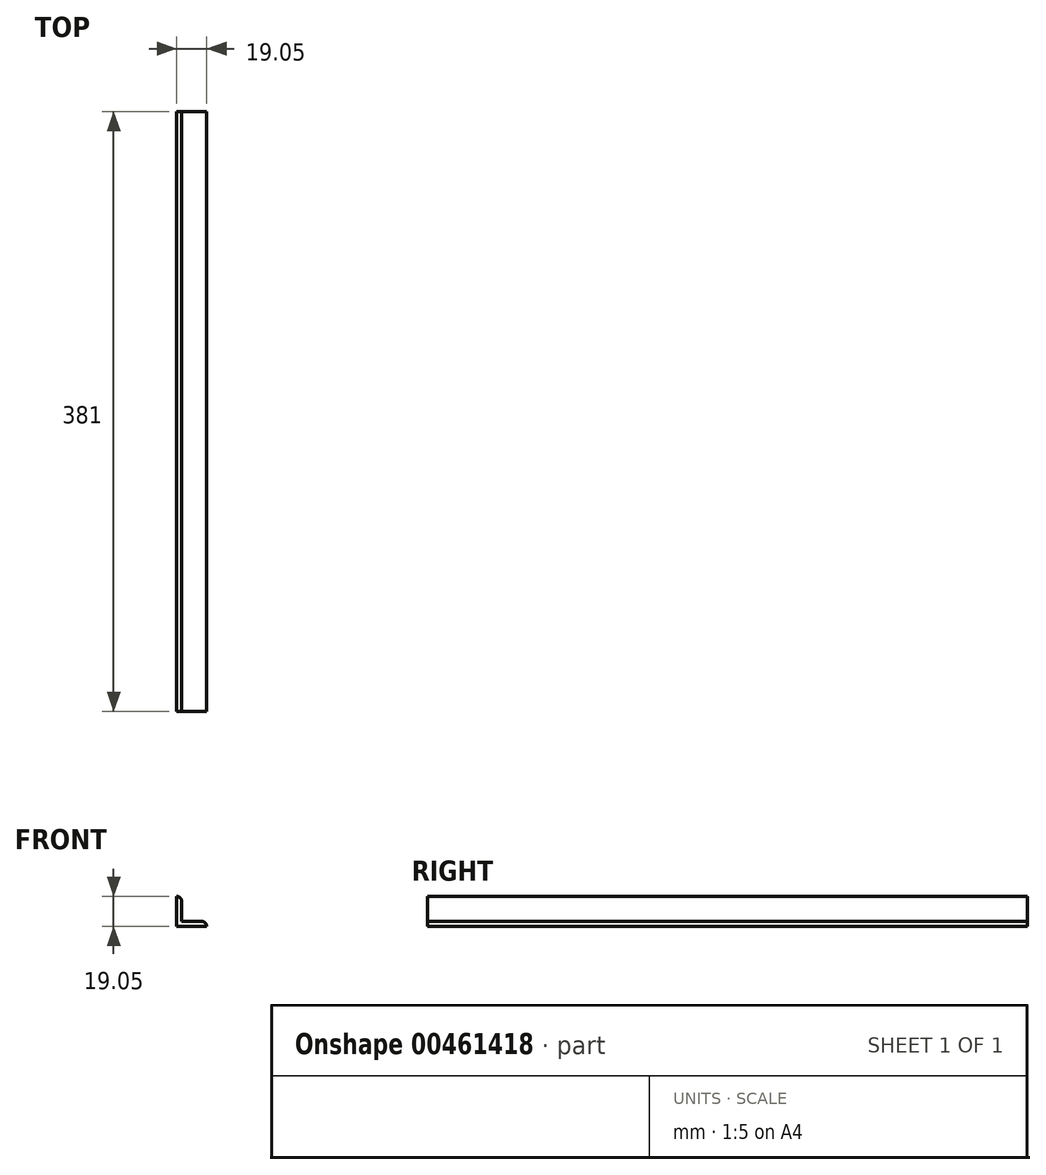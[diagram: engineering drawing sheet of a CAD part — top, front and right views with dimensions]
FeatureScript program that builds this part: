
annotation { "Feature Type Name" : "Feature", "Feature Type Description" : "" }
export const myFeature = defineFeature(function(context is Context, id is Id, definition is map)
    precondition{}
    {
        {
            var Q0;
            Q0=qCreatedBy(makeId("Front.planeOp"),FACE);
            var sketch = newSketch(context, id + "F0", { "sketchPlane" : qUnion([Q0])});
            skLineSegment(sketch, "E0", {"start": v(0, 19.05) * mm, "end": v(0, 0) * mm});
            skLineSegment(sketch, "E1", {"start": v(0, 0) * mm, "end": v(19.05, 0) * mm});
            skLineSegment(sketch, "E2", {"start": v(15.88, 3.17) * mm, "end": v(3.18, 3.17) * mm});
            skLineSegment(sketch, "E3", {"start": v(3.17, 3.17) * mm, "end": v(3.17, 15.88) * mm});
            skLineSegment(sketch, "E4", {"start": v(0, 19.05) * mm, "end": v(0, 19.05) * mm});
            skArc(sketch, "E5.filletArc", {"start": v(3.17, 15.88) * mm, "mid": v(2.25, 18.12) * mm, "end": v(0, 19.05) * mm});
            skArc(sketch, "E6.filletArc", {"start": v(19.05, 0) * mm, "mid": v(18.12, 2.25) * mm, "end": v(15.88, 3.18) * mm});
            skSolve(sketch);
        }
        {
            var Q0;
            Q0=qSketchRegion(id+"F0",true);
            extrude(context, id + "F1", {"entities" : qUnion([Q0]), "endBound" : BoundingType.SYMMETRIC, "depth" : 381 * mm});
        }
    });
